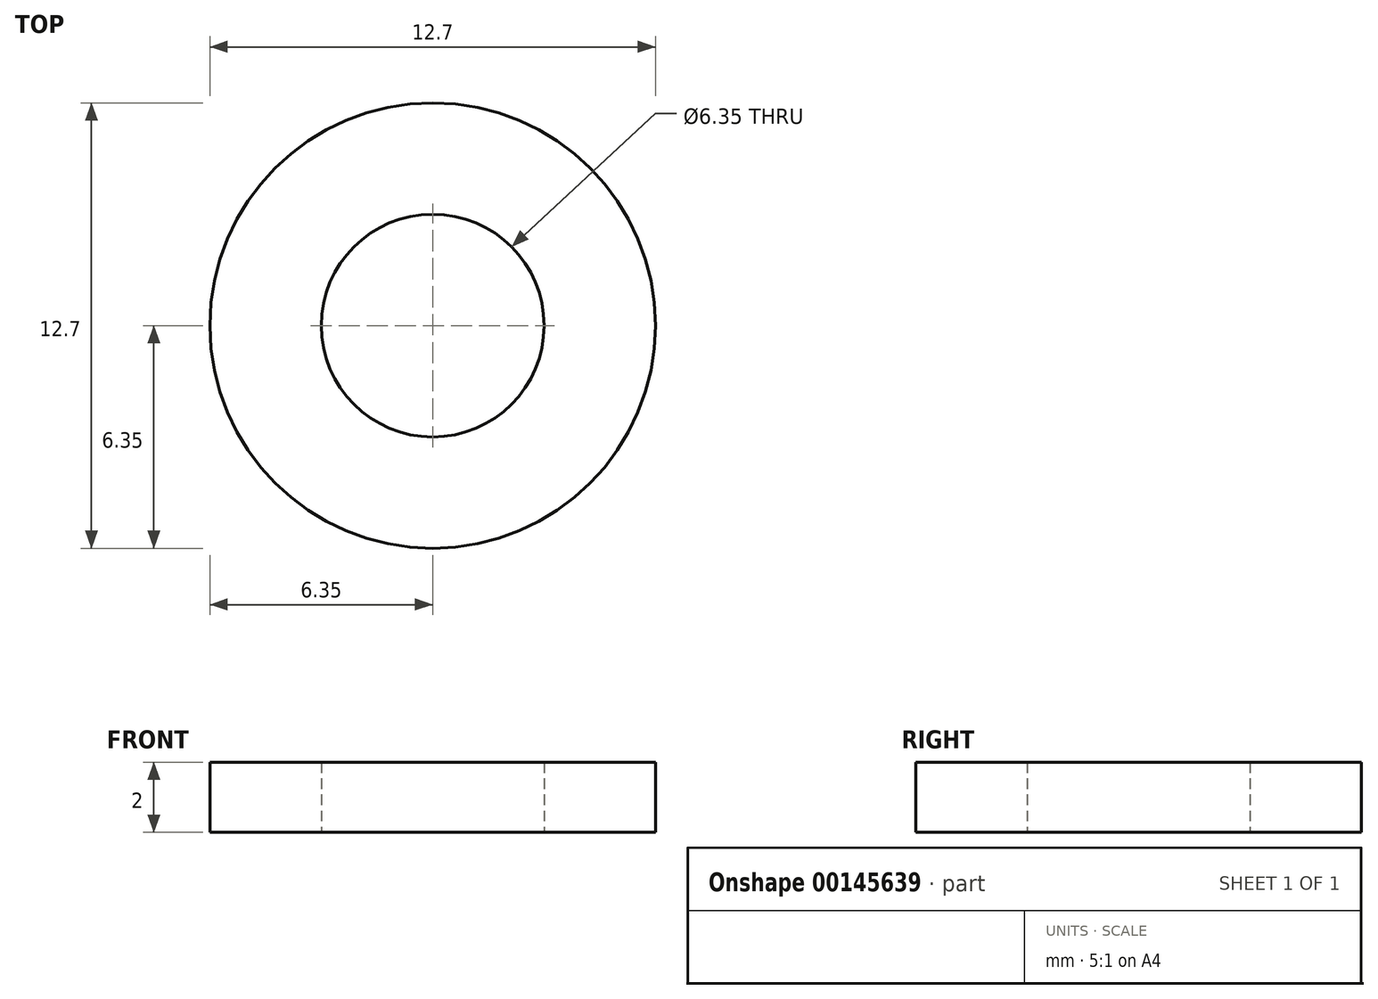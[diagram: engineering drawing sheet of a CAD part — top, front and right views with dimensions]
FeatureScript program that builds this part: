
annotation { "Feature Type Name" : "Feature", "Feature Type Description" : "" }
export const myFeature = defineFeature(function(context is Context, id is Id, definition is map)
    precondition{}
    {
        {
            var Q0;
            Q0=qCreatedBy(makeId("Top.planeOp"),FACE);
            var sketch = newSketch(context, id + "F0", { "sketchPlane" : qUnion([Q0])});
            skCircle(sketch, "E0", {"center": v(0, 0) * mm, "radius": 3.18 * mm});
            skCircle(sketch, "E1", {"center": v(0, 0) * mm, "radius": 6.35 * mm});
            skSolve(sketch);
        }
        {
            var Q0;
            Q0=makeQuery(id+"F0.imprint","IMPRINT",FACE,{"disambiguationData":[TD([[makeQuery(id+"F0.imprint","IMPRINT",EDGE,{"derivedFrom":sQuery(id+"F0.wireOp",EDGE,"E0")}),-1.0]])]});
            extrude(context, id + "F1", {"entities" : qUnion([Q0]), "depth" : 2 * mm});
        }
    });
